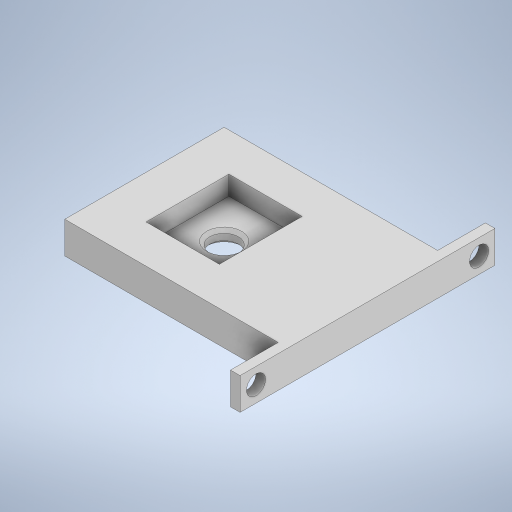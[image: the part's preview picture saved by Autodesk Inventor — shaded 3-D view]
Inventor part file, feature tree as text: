
AUTODESK INVENTOR PART (.ipt)
format: ipt  version: 2023 (Build 270158000, 158)  size: 284,160 bytes
history: native  units: mm
features: extrude x3, sketch x3, other x1, chamfer x1
ambient origin geometry x8: Origin, YZ Plane, XZ Plane, XY Plane, X Axis, Y Axis, Z Axis, Center Point
bodies: Body1 (feature_tree)
feature tree (8):
  other  "Твердое тело1"
  extrude  "Выдавливание1"  Depth=70.0mm
  extrude  "Выдавливание2"  Depth=50.0mm
  chamfer  "Фаска1"  Distance=45.0mm
  extrude  "Выдавливание4"  Depth=25.0mm
  sketch  "Эскиз1"
  sketch  "Эскиз2"
  sketch  "Эскиз4"
